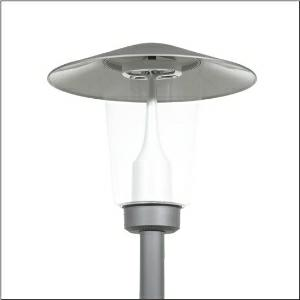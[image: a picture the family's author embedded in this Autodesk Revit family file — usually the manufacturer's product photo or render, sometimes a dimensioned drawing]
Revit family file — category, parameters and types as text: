
# Revit family: pilzleuchte_iq___p1_0a_5xa5235nf14hp_8191
name_source: partatom
category: Lighting Fixtures
units: mm (PartAtom-declared; Revit-internal decimal feet)

## family parameters
Cut with Voids When Loaded = No
Host = Face
Light Source = No
Part Type = Normal
Room Calculation Point = No
Round Connector Dimension = Use Diameter
Shared = No

## types (1)
- --- (1 x LED, 4250 lm, 33.6 W, 2700K)
    Apparent Load = 34 VA
    CIE Flux Codes = 35 64 90 96 100
    Color Rendering = 70
    Color Temperature = 2700K
    Default Elevation = 1800 mm
    Description = Mushroom Luminaire iQ, mast luminaire, Module 540 iQ-SR, primary light control with 3 zone facetted reflector, of plastic, silver coated, highly specular, structured, primary optical cover: cover, of PMMA, transparent, light distribution: P1.0a, light emission: direct distribution, primary light characteristic: strongly asymmetric, installation type: post-top, LED, High Power LED, rated luminous flux: 4.250lm, luminous efficacy: 127lm/W, light colour: 727, colour temperature: 2700K, control gear: iQ Street-Remote, control: pre-setting: logarithmic dimming characteristic, Street-Remote, Auto-Match, Temp-Guard, Lumen-Switch, Night-Set, Smart-Wire, Light-Fading, Desk-Remote (wireless, voltage-free reading and setting of iQ features in the workshop via application-optimized NFC function/RFID function), optimised constant luminous flux control (CLO 2.0), with terminal, 6-pole, max. 2.5mm², mains connection: 230..240V, AC, 50/60Hz, start of lifetime: 34W, end of service life: 36W, reduction: 15W, luminaire housing, upper part, of glass-fibre reinforced polyester, coated, Siteco® metallic grey (DB 702S), diameter: 650mm, height: 586mm, spigot size: d x l = 76 x 70mm (post-top) | with reducer (optional accessory) 60 x 70mm, mounting height: 3..5m, post-top mast mounting element, of diecast aluminium, coated, Siteco® metallic grey (DB 702S), Module 540 iQ-SR, traffic white (RAL 9016), equipment: Power, protection rating (complete): IP65, insulation class (complete): insulation class II (safety insulation), certification: CE, ENEC, VDE, packaging unit: 1 piece

Light Distribution: P1.0a
    Height = 586 mm
    Lamp = 1 x LED
    Lamp Light Flux = 4250 lm
    Lamp Power = 33.6 W
    Lamp count = 1
    Length = 650 mm
    Luminous efficacy = 126 lm/W
    Manufacturer = Siteco
    ModVariant = No
    Model = 5XA5235NF14HP
    Number of Poles = 1
    OnlyDefault = Yes
    Power Factor = 1
    Product Name = Pilzleuchte iQ | P1.0a
    Product group = mast luminaire | pylon top
    ProductGroupID = 6100
    Protection Class = Protection class II
    Protection Degree = IP 65
    RLX_Detail_Level = 1
    RLX_Emergency_Light_Flux = 0 lm
    RLX_Emergency_Type = 0
    RLX_Emergency_Type_DB = No
    RlxData = <blob elided: 51885 chars, md5=dd777b43>
    Socket = socket
    Standby Power = 0 W
    System Light Flux = 4250 lm
    System Power = 34 W
    Type Comments = factory setting: luminous flux: 100 % | dim-lin: 254 | 695 mA
    Type Image = l_1006077.jpg
    URL = http://relux.com
    VarID = @adj_173767
    Voltage = 0 V
    Weight = 0.00 kg
    Width = 0 mm  [stored 0 ft]

note: [stored X ft] marks values corroborated as IEEE doubles in the binary element streams (Revit-internal decimal feet)

## geometry (parser evidence)
native form markers: Blend x4, Sweep x14
no freeform markers — native parametric forms only
